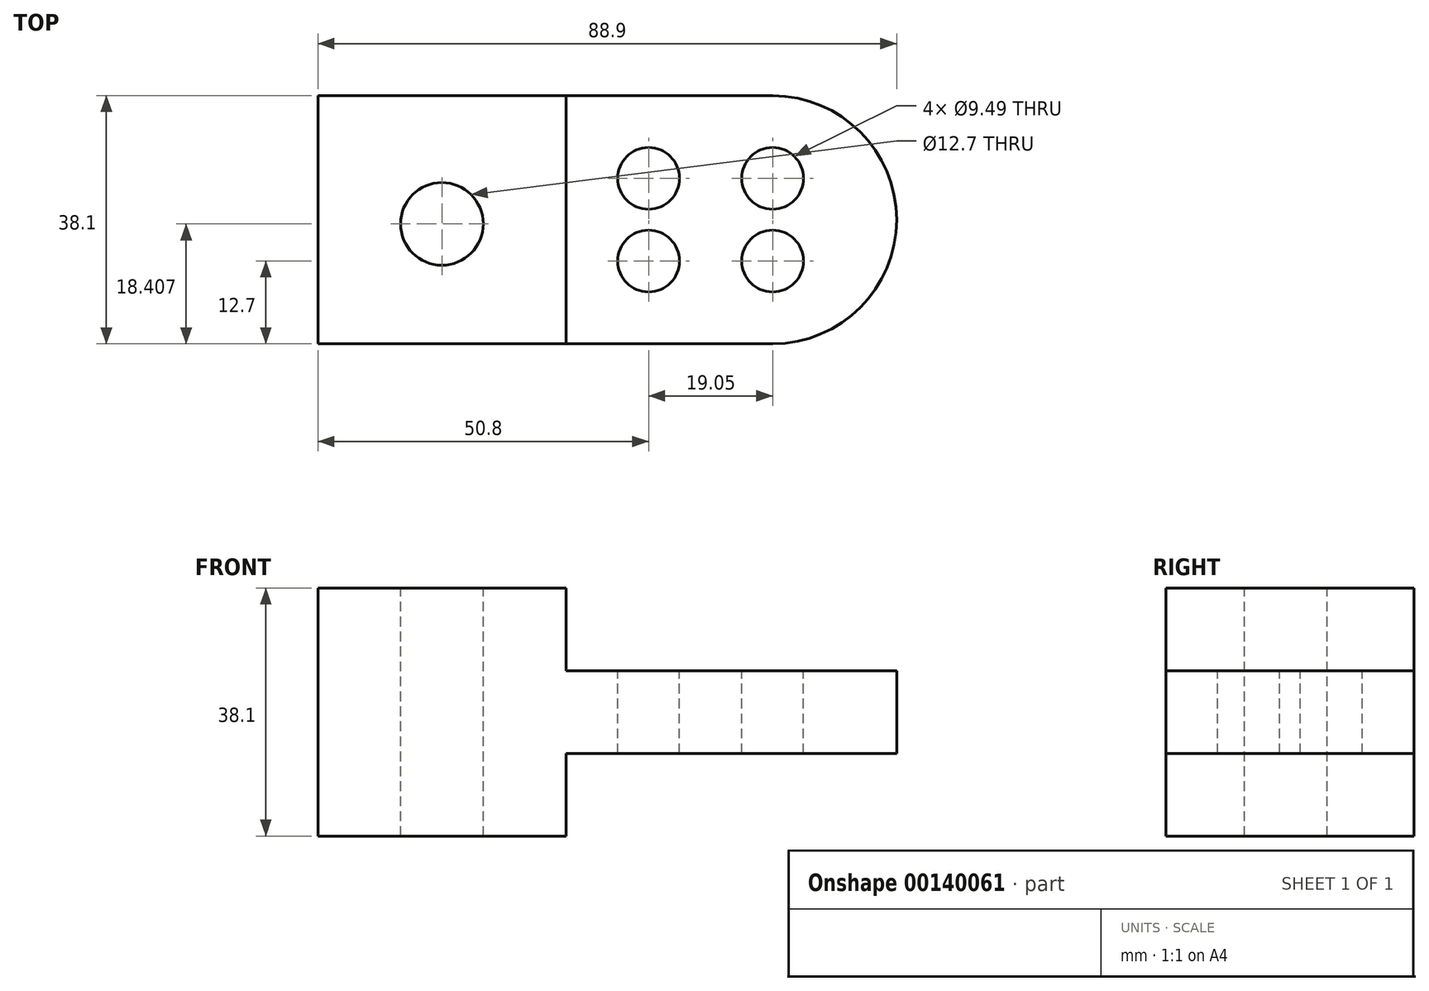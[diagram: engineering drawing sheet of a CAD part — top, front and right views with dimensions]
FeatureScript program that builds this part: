
annotation { "Feature Type Name" : "Feature", "Feature Type Description" : "" }
export const myFeature = defineFeature(function(context is Context, id is Id, definition is map)
    precondition{}
    {
        {
            var Q0;
            Q0=qCreatedBy(makeId("Front.planeOp"),FACE);
            var sketch = newSketch(context, id + "F0", { "sketchPlane" : qUnion([Q0])});
            skLineSegment(sketch, "E0", {"start": v(0, 0) * mm, "end": v(0, 38.1) * mm});
            skLineSegment(sketch, "E1", {"start": v(0, 38.1) * mm, "end": v(38.1, 38.1) * mm});
            skLineSegment(sketch, "E2", {"start": v(38.1, 38.1) * mm, "end": v(38.1, 25.4) * mm});
            skLineSegment(sketch, "E3", {"start": v(38.1, 25.4) * mm, "end": v(69.85, 25.4) * mm});
            skLineSegment(sketch, "E4", {"start": v(69.85, 25.4) * mm, "end": v(69.85, 12.7) * mm});
            skLineSegment(sketch, "E5", {"start": v(69.85, 12.7) * mm, "end": v(38.1, 12.7) * mm});
            skLineSegment(sketch, "E6", {"start": v(38.1, 12.7) * mm, "end": v(38.1, 0) * mm});
            skLineSegment(sketch, "E7", {"start": v(38.1, 0) * mm, "end": v(0, 0) * mm});
            skSolve(sketch);
        }
        {
            var Q0;
            Q0=makeQuery(id+"F0.imprint","IMPRINT",FACE,{"disambiguationData":[TD([[makeQuery(id+"F0.imprint","IMPRINT",EDGE,{"derivedFrom":sQuery(id+"F0.wireOp",EDGE,"E0")}),-1.0]])]});
            extrude(context, id + "F1", {"entities" : qUnion([Q0]), "depth" : 38.1 * mm});
        }
        {
            var Q0;
            Q0=makeQuery(id+"F1.opExtrude","SWEPT_FACE",FACE,{"disambiguationData":[OSD([sQuery(id+"F0.wireOp",EDGE,"E3")])]});
            var sketch = newSketch(context, id + "F2", { "sketchPlane" : qUnion([Q0])});
            skArc(sketch, "E8", {"start": v(69.85, -38.1) * mm, "mid": v(88.9, -19.05) * mm, "end": v(69.85, 0) * mm});
            skLineSegment(sketch, "E9", {"start": v(69.85, 0) * mm, "end": v(69.85, -38.1) * mm, "construction": true});
            skSolve(sketch);
        }
        {
            var Q0;
            Q0=makeQuery(id+"F2.imprint","IMPRINT",FACE,{"disambiguationData":[TD([[makeQuery(id+"F2.imprint","IMPRINT",EDGE,{"derivedFrom":sQuery(id+"F2.wireOp",EDGE,"62b6dc8c-e77e-4b4f-8efe-552848070e0a.0")}),-1.0]])]});
            var Q1;
            Q1=makeQuery(id+"F2.imprint","IMPRINT",FACE,{"disambiguationData":[TD([[makeQuery(id+"F2.imprint","IMPRINT",EDGE,{"derivedFrom":sQuery(id+"F2.wireOp",EDGE,"E8")}),1.0]])]});
            extrude(context, id + "F3", {"entities" : qUnion([Q0, Q1]), "operationType" : NewBodyOperationType.ADD, "oppositeDirection" : true, "depth" : 12.7 * mm});
        }
        {
            var Q0;
            Q0=makeQuery(id+"F1.opExtrude","SWEPT_FACE",FACE,{"disambiguationData":[OSD([sQuery(id+"F0.wireOp",EDGE,"E1")])]});
            var sketch = newSketch(context, id + "F4", { "sketchPlane" : qUnion([Q0])});
            skCircle(sketch, "E10", {"center": v(19.05, -19.7) * mm, "radius": 6.35 * mm});
            skPoint(sketch, "E10.centerSnap0", {"position": v(19.05, 0) * mm});
            skCircle(sketch, "E11", {"center": v(50.8, -12.7) * mm, "radius": 4.75 * mm});
            skCircle(sketch, "E12.0.1.0", {"center": v(50.8, -25.4) * mm, "radius": 4.75 * mm});
            skCircle(sketch, "E12.1.0.0", {"center": v(69.85, -12.7) * mm, "radius": 4.75 * mm});
            skCircle(sketch, "E12.1.1.0", {"center": v(69.85, -25.4) * mm, "radius": 4.75 * mm});
            skLineSegment(sketch, "E12.direction1", {"start": v(50.8, -12.7) * mm, "end": v(69.85, -12.7) * mm, "construction": true});
            skLineSegment(sketch, "E12.direction2", {"start": v(50.8, -12.7) * mm, "end": v(50.8, -25.4) * mm, "construction": true});
            skSolve(sketch);
        }
        {
            var Q0;
            Q0=makeQuery(id+"F4.imprint","IMPRINT",FACE,{"disambiguationData":[TD([[makeQuery(id+"F4.imprint","IMPRINT",EDGE,{"derivedFrom":sQuery(id+"F4.wireOp",EDGE,"E10")}),1.0]])]});
            var Q1;
            Q1=makeQuery(id+"F4.imprint","IMPRINT",FACE,{"disambiguationData":[TD([[makeQuery(id+"F4.imprint","IMPRINT",EDGE,{"derivedFrom":sQuery(id+"F4.wireOp",EDGE,"E11")}),1.0]])]});
            var Q2;
            Q2=makeQuery(id+"F4.imprint","IMPRINT",FACE,{"disambiguationData":[TD([[makeQuery(id+"F4.imprint","IMPRINT",EDGE,{"derivedFrom":sQuery(id+"F4.wireOp",EDGE,"E12.0.1.0")}),1.0]])]});
            var Q3;
            Q3=makeQuery(id+"F4.imprint","IMPRINT",FACE,{"disambiguationData":[TD([[makeQuery(id+"F4.imprint","IMPRINT",EDGE,{"derivedFrom":sQuery(id+"F4.wireOp",EDGE,"E12.1.1.0")}),1.0]])]});
            var Q4;
            Q4=makeQuery(id+"F4.imprint","IMPRINT",FACE,{"disambiguationData":[TD([[makeQuery(id+"F4.imprint","IMPRINT",EDGE,{"derivedFrom":sQuery(id+"F4.wireOp",EDGE,"E12.1.0.0")}),1.0]])]});
            extrude(context, id + "F5", {"entities" : qUnion([Q0, Q1, Q2, Q3, Q4]), "operationType" : NewBodyOperationType.REMOVE, "endBound" : BoundingType.THROUGH_ALL, "oppositeDirection" : true, "depth" : 25.4 * mm});
        }
    });
